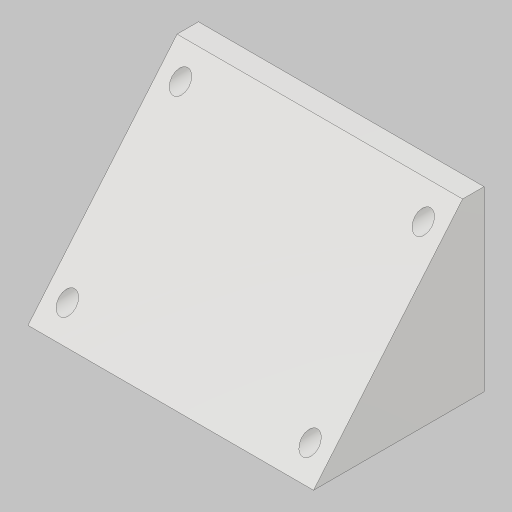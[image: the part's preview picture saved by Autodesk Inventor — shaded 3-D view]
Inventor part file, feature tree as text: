
AUTODESK INVENTOR PART (.ipt)
format: ipt  version: 2023.5 (Build 275446000, 446)  size: 112,128 bytes
history: native  units: in
note: dims shown in document units (in); Inventor stores cm internally (conversion verified against a paired STEP export)
features: sketch x2, extrude x2, hole x1
ambient origin geometry x8: Origin, YZ Plane, XZ Plane, XY Plane, X Axis, Y Axis, Z Axis, Center Point
bodies: Solid1 (feature_tree)
feature tree (5):
  sketch  "Sketch1"  dims[d0=2.8346in d1=1.5748in]
  extrude  "Extrusion1"  Depth=1.5748in
  extrude  "Extrusion2"  Depth=0.25in
  hole  "Hole2"  [1 undecoded]
  sketch  "Sketch2"  dims[d2=0.25in d3=0.25in d4=0.25in d5=0.0in d13=0.2749in d15=0.25in d16=0.0in d17=0.201in d18=0.75in d19=0.375in d20=0.25in d21=0.5635in d22=1.0in d23=0.8108in]
note: 1 required parameter value undecoded (feature->parameter linkage not recoverable at this tier; creation-order binding heuristic only, values carry confidence <= 0.55)
